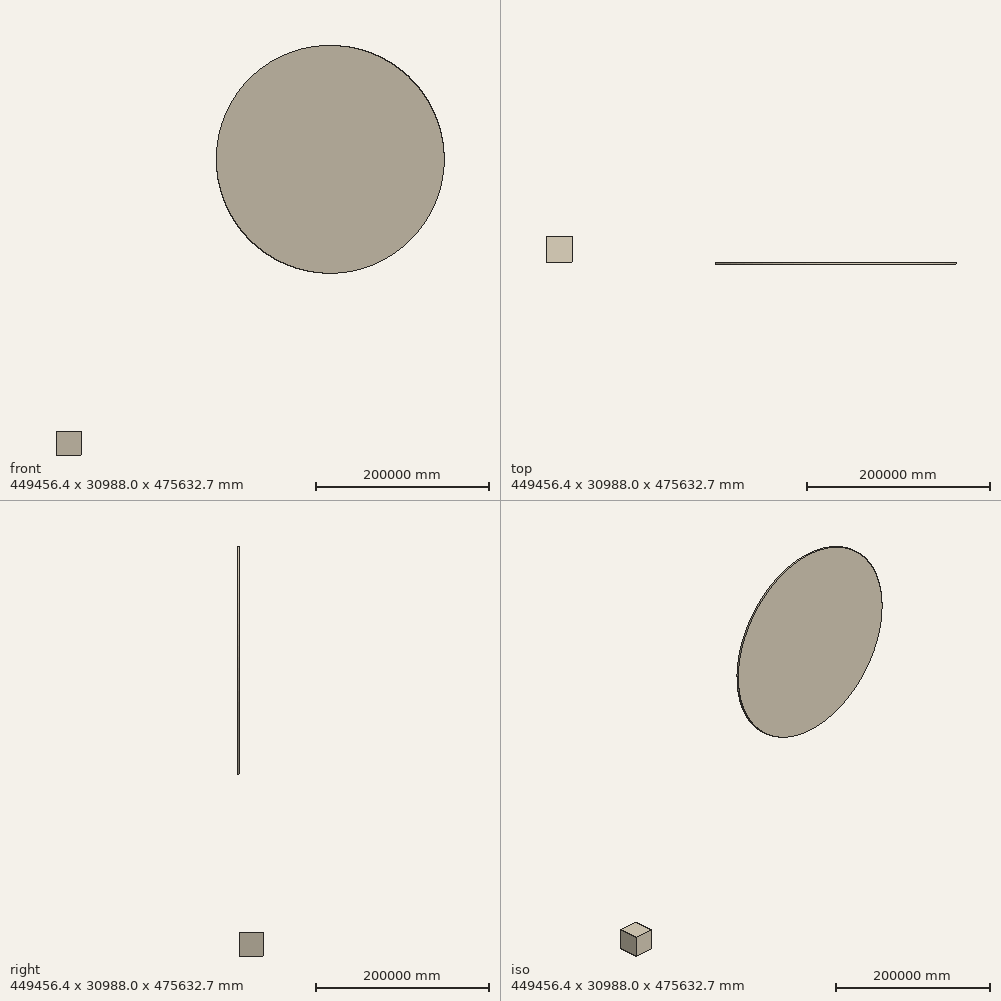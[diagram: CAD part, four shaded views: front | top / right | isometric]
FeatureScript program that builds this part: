
annotation { "Feature Type Name" : "Feature", "Feature Type Description" : "" }
export const myFeature = defineFeature(function(context is Context, id is Id, definition is map)
    precondition{}
    {
        {
            var Q0;
            Q0=qCreatedBy(makeId("Front.planeOp"),FACE);
            var sketch = newSketch(context, id + "F0", { "sketchPlane" : qUnion([Q0])});
            skLineSegment(sketch, "E0.bottom", {"start": v(-481.34, -157.95) * mm, "end": v(-375.42, -157.95) * mm});
            skLineSegment(sketch, "E0.top", {"start": v(-481.34, -331.36) * mm, "end": v(-375.42, -331.36) * mm});
            skLineSegment(sketch, "E0.left", {"start": v(-481.34, -157.95) * mm, "end": v(-481.34, -331.36) * mm});
            skLineSegment(sketch, "E0.right", {"start": v(-375.42, -157.95) * mm, "end": v(-375.42, -331.36) * mm});
            skSolve(sketch);
        }
        {
            var Q0;
            Q0=makeQuery(id+"F0.imprint","IMPRINT",FACE,{"disambiguationData":[TD([[makeQuery(id+"F0.imprint","IMPRINT",EDGE,{"derivedFrom":sQuery(id+"F0.wireOp",EDGE,"E0.bottom")}),-1.0]])]});
            extrude(context, id + "F1", {"entities" : qUnion([Q0]), "depth" : 508 * mm});
        }
        {
            var Q0;
            Q0=makeQuery(id+"F1.opExtrude","SWEPT_FACE",FACE,{"disambiguationData":[OSD([sQuery(id+"F0.wireOp",EDGE,"E0.bottom")])]});
            extrude(context, id + "F2", {"entities" : qUnion([Q0]), "operationType" : NewBodyOperationType.ADD, "depth" : 254 * mm});
        }
        {
            var Q0;
            {var subQ0=sQuery(id+"F0.wireOp",EDGE,"E0.right");Q0=makeQuery(id+"F2.boolean.opBoolean","MERGE",FACE,{"derivedFrom":[makeQuery(id+"F1.opExtrude","SWEPT_FACE",FACE,{"disambiguationData":[OSD([subQ0])]}),makeQuery(id+"F2.opExtrude","SWEPT_FACE",FACE,{"disambiguationData":[OSD([sQuery(id+"F0.wireOp",EDGE,"E0.bottom"),subQ0])]})]});}
            extrude(context, id + "F3", {"entities" : qUnion([Q0]), "operationType" : NewBodyOperationType.ADD, "depth" : 254 * mm});
        }
        {
            var Q0;
            {var subQ0=sQuery(id+"F0.wireOp",EDGE,"E0.right");var subQ1=sQuery(id+"F0.wireOp",EDGE,"E0.bottom");Q0=makeQuery(id+"F3.boolean.opBoolean","MERGE",FACE,{"derivedFrom":[makeQuery(id+"F2.opExtrude","CAP_FACE",FACE,{"disambiguationData":[OSD([subQ1])],"isStart":false}),makeQuery(id+"F3.opExtrude","SWEPT_FACE",FACE,{"disambiguationData":[OSD([subQ1,subQ0]),TDD([makeQuery(id+"F2.opExtrude","CAP_EDGE",EDGE,{"disambiguationData":[OSD([subQ1,subQ0])],"isStart":false})])]})]});}
            extrude(context, id + "F4", {"entities" : qUnion([Q0]), "operationType" : NewBodyOperationType.ADD, "depth" : 2540 * mm});
        }
        {
            var Q0;
            {var subQ0=sQuery(id+"F0.wireOp",EDGE,"E0.right");var subQ1=sQuery(id+"F0.wireOp",EDGE,"E0.bottom");Q0=makeQuery(id+"F4.boolean.opBoolean","MERGE",FACE,{"derivedFrom":[makeQuery(id+"F3.opExtrude","CAP_FACE",FACE,{"disambiguationData":[OSD([subQ1,subQ0])],"isStart":false}),makeQuery(id+"F4.opExtrude","SWEPT_FACE",FACE,{"disambiguationData":[OSD([subQ1,subQ0]),TDD([makeQuery(id+"F3.opExtrude","CAP_EDGE",EDGE,{"disambiguationData":[OSD([subQ1,subQ0]),TDD([makeQuery(id+"F2.opExtrude","CAP_EDGE",EDGE,{"disambiguationData":[OSD([subQ1,subQ0])],"isStart":false})])],"isStart":false})])]})]});}
            extrude(context, id + "F5", {"entities" : qUnion([Q0]), "operationType" : NewBodyOperationType.ADD, "depth" : 2540 * mm});
        }
        {
            var Q0;
            {var subQ0=sQuery(id+"F0.wireOp",EDGE,"E0.right");var subQ1=sQuery(id+"F0.wireOp",EDGE,"E0.bottom");var subQ2=makeQuery(id+"F1.opExtrude","CAP_VERTEX",VERTEX,{"disambiguationData":[OSD([subQ1,subQ0])],"isStart":false});var subQ3=makeQuery(id+"F2.opExtrude","CAP_VERTEX",VERTEX,{"disambiguationData":[OSD([subQ1,subQ0]),TDD([subQ2])],"isStart":false});var subQ4=makeQuery(id+"F2.boolean.opBoolean","MERGE",EDGE,{"derivedFrom":[makeQuery(id+"F1.opExtrude","CAP_EDGE",EDGE,{"disambiguationData":[OSD([subQ0])],"isStart":false}),makeQuery(id+"F2.opExtrude","SWEPT_EDGE",EDGE,{"disambiguationData":[OSD([subQ1,subQ0]),TDD([subQ2])]})]});var subQ5=makeQuery(id+"F1.opExtrude","CAP_EDGE",EDGE,{"disambiguationData":[OSD([subQ1])],"isStart":false});Q0=makeQuery(id+"F5.boolean.opBoolean","MERGE",FACE,{"derivedFrom":[makeQuery(id+"F4.boolean.opBoolean","MERGE",FACE,{"derivedFrom":[makeQuery(id+"F3.boolean.opBoolean","MERGE",FACE,{"derivedFrom":[makeQuery(id+"F2.boolean.opBoolean","MERGE",FACE,{"derivedFrom":[makeQuery(id+"F1.opExtrude","CAP_FACE",FACE,{"disambiguationData":[OSD([subQ1,sQuery(id+"F0.wireOp",EDGE,"E0.top"),sQuery(id+"F0.wireOp",EDGE,"E0.left"),subQ0])],"isStart":false}),makeQuery(id+"F2.opExtrude","SWEPT_FACE",FACE,{"disambiguationData":[OSD([subQ1]),TDD([subQ5])]})]}),makeQuery(id+"F3.opExtrude","SWEPT_FACE",FACE,{"disambiguationData":[OSD([subQ1,subQ0]),TDD([subQ4])]})]}),makeQuery(id+"F4.opExtrude","SWEPT_FACE",FACE,{"disambiguationData":[OSD([subQ1,subQ0]),TDD([makeQuery(id+"F3.boolean.opBoolean","MERGE",EDGE,{"derivedFrom":[makeQuery(id+"F2.opExtrude","CAP_EDGE",EDGE,{"disambiguationData":[OSD([subQ1]),TDD([subQ5])],"isStart":false}),makeQuery(id+"F3.opExtrude","SWEPT_EDGE",EDGE,{"disambiguationData":[OSD([subQ1,subQ0]),TDD([subQ3])]})]})])]})]}),makeQuery(id+"F5.opExtrude","SWEPT_FACE",FACE,{"disambiguationData":[OSD([subQ1,subQ0]),TDD([makeQuery(id+"F4.boolean.opBoolean","MERGE",EDGE,{"derivedFrom":[makeQuery(id+"F3.opExtrude","CAP_EDGE",EDGE,{"disambiguationData":[OSD([subQ1,subQ0]),TDD([subQ4])],"isStart":false}),makeQuery(id+"F4.opExtrude","SWEPT_EDGE",EDGE,{"disambiguationData":[OSD([subQ1,subQ0]),TDD([makeQuery(id+"F3.opExtrude","CAP_VERTEX",VERTEX,{"disambiguationData":[OSD([subQ1,subQ0]),TDD([subQ3])],"isStart":false})])]})]})])]})]});}
            extrude(context, id + "F6", {"entities" : qUnion([Q0]), "operationType" : NewBodyOperationType.ADD, "depth" : 2540 * mm});
        }
        {
            var Q0;
            Q0=makeQuery(id+"F6.opExtrude","CAP_FACE",FACE,{"disambiguationData":[OSD([sQuery(id+"F0.wireOp",EDGE,"E0.bottom"),sQuery(id+"F0.wireOp",EDGE,"E0.top"),sQuery(id+"F0.wireOp",EDGE,"E0.left"),sQuery(id+"F0.wireOp",EDGE,"E0.right")])],"isStart":false});
            extrude(context, id + "F7", {"entities" : qUnion([Q0]), "operationType" : NewBodyOperationType.ADD, "depth" : 25400 * mm});
        }
        {
            var Q0;
            {var subQ0=sQuery(id+"F0.wireOp",EDGE,"E0.right");var subQ1=sQuery(id+"F0.wireOp",EDGE,"E0.bottom");var subQ2=makeQuery(id+"F2.opExtrude","CAP_VERTEX",VERTEX,{"disambiguationData":[OSD([subQ1,subQ0]),TDD([makeQuery(id+"F1.opExtrude","CAP_VERTEX",VERTEX,{"disambiguationData":[OSD([subQ1,subQ0])],"isStart":false})])],"isStart":false});var subQ3=makeQuery(id+"F5.boolean.opBoolean","MERGE",EDGE,{"derivedFrom":[makeQuery(id+"F4.opExtrude","CAP_EDGE",EDGE,{"disambiguationData":[OSD([subQ1,subQ0]),TDD([makeQuery(id+"F3.boolean.opBoolean","MERGE",EDGE,{"derivedFrom":[makeQuery(id+"F2.opExtrude","CAP_EDGE",EDGE,{"disambiguationData":[OSD([subQ1]),TDD([makeQuery(id+"F1.opExtrude","CAP_EDGE",EDGE,{"disambiguationData":[OSD([subQ1])],"isStart":false})])],"isStart":false}),makeQuery(id+"F3.opExtrude","SWEPT_EDGE",EDGE,{"disambiguationData":[OSD([subQ1,subQ0]),TDD([subQ2])]})]})])],"isStart":false}),makeQuery(id+"F5.opExtrude","SWEPT_EDGE",EDGE,{"disambiguationData":[OSD([subQ1,subQ0]),TDD([makeQuery(id+"F4.opExtrude","CAP_VERTEX",VERTEX,{"disambiguationData":[OSD([subQ1,subQ0]),TDD([makeQuery(id+"F3.opExtrude","CAP_VERTEX",VERTEX,{"disambiguationData":[OSD([subQ1,subQ0]),TDD([subQ2])],"isStart":false})])],"isStart":false})])]})]});Q0=makeQuery(id+"F7.boolean.opBoolean","MERGE",FACE,{"derivedFrom":[makeQuery(id+"F6.boolean.opBoolean","MERGE",FACE,{"derivedFrom":[makeQuery(id+"F5.boolean.opBoolean","MERGE",FACE,{"derivedFrom":[makeQuery(id+"F4.opExtrude","CAP_FACE",FACE,{"disambiguationData":[OSD([subQ1,subQ0])],"isStart":false}),makeQuery(id+"F5.opExtrude","SWEPT_FACE",FACE,{"disambiguationData":[OSD([subQ1,subQ0]),TDD([makeQuery(id+"F4.opExtrude","CAP_EDGE",EDGE,{"disambiguationData":[OSD([subQ1,subQ0]),TDD([makeQuery(id+"F3.opExtrude","CAP_EDGE",EDGE,{"disambiguationData":[OSD([subQ1,subQ0]),TDD([makeQuery(id+"F2.opExtrude","CAP_EDGE",EDGE,{"disambiguationData":[OSD([subQ1,subQ0])],"isStart":false})])],"isStart":false})])],"isStart":false})])]})]}),makeQuery(id+"F6.opExtrude","SWEPT_FACE",FACE,{"disambiguationData":[OSD([subQ1,subQ0]),TDD([subQ3])]})]}),makeQuery(id+"F7.opExtrude","SWEPT_FACE",FACE,{"disambiguationData":[OSD([subQ1,subQ0]),TDD([makeQuery(id+"F6.opExtrude","CAP_EDGE",EDGE,{"disambiguationData":[OSD([subQ1,subQ0]),TDD([subQ3])],"isStart":false})])]})]});}
            extrude(context, id + "F8", {"entities" : qUnion([Q0]), "operationType" : NewBodyOperationType.ADD, "depth" : 25400 * mm});
        }
        {
            var Q0;
            {var subQ0=sQuery(id+"F0.wireOp",EDGE,"E0.right");var subQ1=sQuery(id+"F0.wireOp",EDGE,"E0.bottom");var subQ2=makeQuery(id+"F1.opExtrude","CAP_VERTEX",VERTEX,{"disambiguationData":[OSD([subQ1,subQ0])],"isStart":false});var subQ3=makeQuery(id+"F5.opExtrude","CAP_EDGE",EDGE,{"disambiguationData":[OSD([subQ1,subQ0]),TDD([makeQuery(id+"F4.boolean.opBoolean","MERGE",EDGE,{"derivedFrom":[makeQuery(id+"F3.opExtrude","CAP_EDGE",EDGE,{"disambiguationData":[OSD([subQ1,subQ0]),TDD([makeQuery(id+"F2.boolean.opBoolean","MERGE",EDGE,{"derivedFrom":[makeQuery(id+"F1.opExtrude","CAP_EDGE",EDGE,{"disambiguationData":[OSD([subQ0])],"isStart":false}),makeQuery(id+"F2.opExtrude","SWEPT_EDGE",EDGE,{"disambiguationData":[OSD([subQ1,subQ0]),TDD([subQ2])]})]})])],"isStart":false}),makeQuery(id+"F4.opExtrude","SWEPT_EDGE",EDGE,{"disambiguationData":[OSD([subQ1,subQ0]),TDD([makeQuery(id+"F3.opExtrude","CAP_VERTEX",VERTEX,{"disambiguationData":[OSD([subQ1,subQ0]),TDD([makeQuery(id+"F2.opExtrude","CAP_VERTEX",VERTEX,{"disambiguationData":[OSD([subQ1,subQ0]),TDD([subQ2])],"isStart":false})])],"isStart":false})])]})]})])],"isStart":false});Q0=makeQuery(id+"F8.boolean.opBoolean","MERGE",FACE,{"derivedFrom":[makeQuery(id+"F7.boolean.opBoolean","MERGE",FACE,{"derivedFrom":[makeQuery(id+"F6.boolean.opBoolean","MERGE",FACE,{"derivedFrom":[makeQuery(id+"F5.opExtrude","CAP_FACE",FACE,{"disambiguationData":[OSD([subQ1,subQ0])],"isStart":false}),makeQuery(id+"F6.opExtrude","SWEPT_FACE",FACE,{"disambiguationData":[OSD([subQ1,subQ0]),TDD([subQ3])]})]}),makeQuery(id+"F7.opExtrude","SWEPT_FACE",FACE,{"disambiguationData":[OSD([subQ1,subQ0]),TDD([makeQuery(id+"F6.opExtrude","CAP_EDGE",EDGE,{"disambiguationData":[OSD([subQ1,subQ0]),TDD([subQ3])],"isStart":false})])]})]}),makeQuery(id+"F8.opExtrude","SWEPT_FACE",FACE,{"disambiguationData":[OSD([subQ1,subQ0]),TDD([makeQuery(id+"F7.boolean.opBoolean","MERGE",EDGE,{"derivedFrom":[makeQuery(id+"F6.boolean.opBoolean","MERGE",EDGE,{"derivedFrom":[makeQuery(id+"F5.opExtrude","CAP_EDGE",EDGE,{"disambiguationData":[OSD([subQ1,subQ0]),TDD([makeQuery(id+"F4.opExtrude","CAP_EDGE",EDGE,{"disambiguationData":[OSD([subQ1,subQ0]),TDD([makeQuery(id+"F3.opExtrude","CAP_EDGE",EDGE,{"disambiguationData":[OSD([subQ1,subQ0]),TDD([makeQuery(id+"F2.opExtrude","CAP_EDGE",EDGE,{"disambiguationData":[OSD([subQ1,subQ0])],"isStart":false})])],"isStart":false})])],"isStart":false})])],"isStart":false}),makeQuery(id+"F6.opExtrude","SWEPT_EDGE",EDGE,{"disambiguationData":[OSD([subQ1,subQ0])]})]}),makeQuery(id+"F7.opExtrude","SWEPT_EDGE",EDGE,{"disambiguationData":[OSD([subQ1,subQ0])]})]})])]})]});}
            extrude(context, id + "F9", {"entities" : qUnion([Q0]), "operationType" : NewBodyOperationType.ADD, "depth" : 25400 * mm});
        }
        {
            var Q0;
            Q0=makeQuery(id+"F9.opExtrude","CAP_FACE",FACE,{"disambiguationData":[OSD([sQuery(id+"F0.wireOp",EDGE,"E0.bottom"),sQuery(id+"F0.wireOp",EDGE,"E0.right")])],"isStart":false});
            var sketch = newSketch(context, id + "F10", { "sketchPlane" : qUnion([Q0])});
            skSolve(sketch);
        }
        {
            var Q0;
            {var subQ0=sQuery(id+"F0.wireOp",EDGE,"E0.right");Q0=makeQuery(id+"F10.imprint","IMPRINT",FACE,{"disambiguationData":[TD([[makeQuery(id+"F10.imprint","IMPRINT",EDGE,{"derivedFrom":makeQuery(id+"F9.opExtrude","CAP_EDGE",EDGE,{"disambiguationData":[OSD([sQuery(id+"F0.wireOp",EDGE,"E0.top"),subQ0])],"isStart":false})}),1.0]])]});}
            var sketch = newSketch(context, id + "F11", { "sketchPlane" : qUnion([Q0])});
            skSolve(sketch);
        }
        {
            var Q0;
            {var subQ0=sQuery(id+"F0.wireOp",EDGE,"E0.right");Q0=makeQuery(id+"F10.imprint","IMPRINT",FACE,{"disambiguationData":[TD([[makeQuery(id+"F10.imprint","IMPRINT",EDGE,{"derivedFrom":makeQuery(id+"F9.opExtrude","CAP_EDGE",EDGE,{"disambiguationData":[OSD([sQuery(id+"F0.wireOp",EDGE,"E0.top"),subQ0])],"isStart":false})}),1.0]])]});}
            extrude(context, id + "F12", {"entities" : qUnion([Q0]), "operationType" : NewBodyOperationType.ADD, "depth" : 25.4 * mm});
        }
        {
            var Q0;
            {var subQ0=sQuery(id+"F0.wireOp",EDGE,"E0.right");var subQ1=sQuery(id+"F0.wireOp",EDGE,"E0.bottom");var subQ2=makeQuery(id+"F8.opExtrude","CAP_EDGE",EDGE,{"disambiguationData":[OSD([subQ1,subQ0]),TDD([makeQuery(id+"F7.boolean.opBoolean","MERGE",EDGE,{"derivedFrom":[makeQuery(id+"F6.boolean.opBoolean","MERGE",EDGE,{"derivedFrom":[makeQuery(id+"F5.opExtrude","CAP_EDGE",EDGE,{"disambiguationData":[OSD([subQ1,subQ0]),TDD([makeQuery(id+"F4.opExtrude","CAP_EDGE",EDGE,{"disambiguationData":[OSD([subQ1,subQ0]),TDD([makeQuery(id+"F3.opExtrude","CAP_EDGE",EDGE,{"disambiguationData":[OSD([subQ1,subQ0]),TDD([makeQuery(id+"F2.opExtrude","CAP_EDGE",EDGE,{"disambiguationData":[OSD([subQ1,subQ0])],"isStart":false})])],"isStart":false})])],"isStart":false})])],"isStart":false}),makeQuery(id+"F6.opExtrude","SWEPT_EDGE",EDGE,{"disambiguationData":[OSD([subQ1,subQ0])]})]}),makeQuery(id+"F7.opExtrude","SWEPT_EDGE",EDGE,{"disambiguationData":[OSD([subQ1,subQ0])]})]})])],"isStart":false});Q0=makeQuery(id+"F12.boolean.opBoolean","MERGE",FACE,{"derivedFrom":[makeQuery(id+"F9.boolean.opBoolean","MERGE",FACE,{"derivedFrom":[makeQuery(id+"F8.opExtrude","CAP_FACE",FACE,{"disambiguationData":[OSD([subQ1,subQ0])],"isStart":false}),makeQuery(id+"F9.opExtrude","SWEPT_FACE",FACE,{"disambiguationData":[OSD([subQ1,subQ0]),TDD([subQ2])]})]}),makeQuery(id+"F12.opExtrude","SWEPT_FACE",FACE,{"disambiguationData":[OSD([subQ1,subQ0]),TDD([makeQuery(id+"F10.imprint","IMPRINT",EDGE,{"derivedFrom":makeQuery(id+"F9.opExtrude","CAP_EDGE",EDGE,{"disambiguationData":[OSD([subQ1,subQ0]),TDD([subQ2])],"isStart":false})})])]})]});}
            var sketch = newSketch(context, id + "F13", { "sketchPlane" : qUnion([Q0])});
            skSolve(sketch);
        }
        {
            var Q0;
            {var subQ0=sQuery(id+"F0.wireOp",EDGE,"E0.bottom");Q0=makeQuery(id+"F13.imprint","IMPRINT",FACE,{"disambiguationData":[TD([[makeQuery(id+"F13.imprint","IMPRINT",EDGE,{"derivedFrom":makeQuery(id+"F8.opExtrude","CAP_EDGE",EDGE,{"disambiguationData":[OSD([subQ0,sQuery(id+"F0.wireOp",EDGE,"E0.left")])],"isStart":false})}),-1.0]])]});}
            var sketch = newSketch(context, id + "F14", { "sketchPlane" : qUnion([Q0])});
            skLineSegment(sketch, "E1.bottom", {"start": v(2166.14, -15440.6) * mm, "end": v(7362.03, -15440.6) * mm});
            skLineSegment(sketch, "E1.top", {"start": v(2166.14, -24936.56) * mm, "end": v(7362.03, -24936.56) * mm});
            skLineSegment(sketch, "E1.left", {"start": v(2166.14, -15440.6) * mm, "end": v(2166.14, -24936.56) * mm});
            skLineSegment(sketch, "E1.right", {"start": v(7362.03, -15440.6) * mm, "end": v(7362.03, -24936.56) * mm});
            skLineSegment(sketch, "E2.bottom", {"start": v(7362.03, -11140.55) * mm, "end": v(17395.49, -11140.55) * mm});
            skLineSegment(sketch, "E2.top", {"start": v(7362.03, -15440.6) * mm, "end": v(17395.49, -15440.6) * mm});
            skLineSegment(sketch, "E2.left", {"start": v(7362.03, -11140.55) * mm, "end": v(7362.03, -15440.6) * mm});
            skLineSegment(sketch, "E2.right", {"start": v(17395.49, -11140.55) * mm, "end": v(17395.49, -15440.6) * mm});
            skLineSegment(sketch, "E3.bottom", {"start": v(17395.49, -15440.6) * mm, "end": v(22322.63, -15440.6) * mm});
            skLineSegment(sketch, "E3.top", {"start": v(17395.49, -24399.05) * mm, "end": v(22322.63, -24399.05) * mm});
            skLineSegment(sketch, "E3.left", {"start": v(17395.49, -15440.6) * mm, "end": v(17395.49, -24399.05) * mm});
            skLineSegment(sketch, "E3.right", {"start": v(22322.63, -15440.6) * mm, "end": v(22322.63, -24399.05) * mm});
            skLineSegment(sketch, "E4.bottom", {"start": v(4047.4, -1734.2) * mm, "end": v(8705.8, -1734.2) * mm});
            skLineSegment(sketch, "E4.top", {"start": v(4047.4, -9169.7) * mm, "end": v(8705.8, -9169.7) * mm});
            skLineSegment(sketch, "E4.left", {"start": v(4047.4, -1734.2) * mm, "end": v(4047.4, -9169.7) * mm});
            skLineSegment(sketch, "E4.right", {"start": v(8705.8, -1734.2) * mm, "end": v(8705.8, -9169.7) * mm});
            skLineSegment(sketch, "E5.bottom", {"start": v(15603.8, -1465.44) * mm, "end": v(20799.7, -1465.44) * mm});
            skLineSegment(sketch, "E5.top", {"start": v(15603.8, -9617.62) * mm, "end": v(20799.7, -9617.62) * mm});
            skLineSegment(sketch, "E5.left", {"start": v(15603.8, -1465.44) * mm, "end": v(15603.8, -9617.62) * mm});
            skLineSegment(sketch, "E5.right", {"start": v(20799.7, -1465.44) * mm, "end": v(20799.7, -9617.62) * mm});
            skSolve(sketch);
        }
        {
            var Q0;
            {var subQ0=sQuery(id+"F0.wireOp",EDGE,"E0.bottom");Q0=makeQuery(id+"F13.imprint","IMPRINT",FACE,{"disambiguationData":[TD([[makeQuery(id+"F13.imprint","IMPRINT",EDGE,{"derivedFrom":makeQuery(id+"F8.opExtrude","CAP_EDGE",EDGE,{"disambiguationData":[OSD([subQ0,sQuery(id+"F0.wireOp",EDGE,"E0.left")])],"isStart":false})}),-1.0]])]});}
            extrude(context, id + "F15", {"entities" : qUnion([Q0]), "operationType" : NewBodyOperationType.ADD, "endBound" : BoundingType.SYMMETRIC, "depth" : 25.4 * mm});
        }
        {
            var Q0;
            {var subQ0=sQuery(id+"F0.wireOp",EDGE,"E0.right");var subQ1=sQuery(id+"F0.wireOp",EDGE,"E0.bottom");var subQ2=makeQuery(id+"F7.opExtrude","CAP_VERTEX",VERTEX,{"disambiguationData":[OSD([subQ1,subQ0])],"isStart":false});var subQ3=makeQuery(id+"F1.opExtrude","CAP_VERTEX",VERTEX,{"disambiguationData":[OSD([subQ1,subQ0])],"isStart":false});var subQ4=makeQuery(id+"F2.opExtrude","CAP_VERTEX",VERTEX,{"disambiguationData":[OSD([subQ1,subQ0]),TDD([subQ3])],"isStart":false});var subQ5=makeQuery(id+"F3.opExtrude","CAP_VERTEX",VERTEX,{"disambiguationData":[OSD([subQ1,subQ0]),TDD([subQ4])],"isStart":false});var subQ6=makeQuery(id+"F8.boolean.opBoolean","MERGE",EDGE,{"derivedFrom":[makeQuery(id+"F7.opExtrude","CAP_EDGE",EDGE,{"disambiguationData":[OSD([subQ1,subQ0]),TDD([makeQuery(id+"F6.opExtrude","CAP_EDGE",EDGE,{"disambiguationData":[OSD([subQ1,subQ0]),TDD([makeQuery(id+"F5.opExtrude","CAP_EDGE",EDGE,{"disambiguationData":[OSD([subQ1,subQ0]),TDD([makeQuery(id+"F4.boolean.opBoolean","MERGE",EDGE,{"derivedFrom":[makeQuery(id+"F3.opExtrude","CAP_EDGE",EDGE,{"disambiguationData":[OSD([subQ1,subQ0]),TDD([makeQuery(id+"F2.boolean.opBoolean","MERGE",EDGE,{"derivedFrom":[makeQuery(id+"F1.opExtrude","CAP_EDGE",EDGE,{"disambiguationData":[OSD([subQ0])],"isStart":false}),makeQuery(id+"F2.opExtrude","SWEPT_EDGE",EDGE,{"disambiguationData":[OSD([subQ1,subQ0]),TDD([subQ3])]})]})])],"isStart":false}),makeQuery(id+"F4.opExtrude","SWEPT_EDGE",EDGE,{"disambiguationData":[OSD([subQ1,subQ0]),TDD([subQ5])]})]})])],"isStart":false})])],"isStart":false})])],"isStart":false}),makeQuery(id+"F8.opExtrude","SWEPT_EDGE",EDGE,{"disambiguationData":[OSD([subQ1,subQ0]),TDD([subQ2])]})]});var subQ7=makeQuery(id+"F9.opExtrude","CAP_EDGE",EDGE,{"disambiguationData":[OSD([subQ1,subQ0]),TDD([subQ6])],"isStart":false});var subQ8=makeQuery(id+"F7.opExtrude","CAP_EDGE",EDGE,{"disambiguationData":[OSD([subQ1,subQ0]),TDD([makeQuery(id+"F6.opExtrude","CAP_EDGE",EDGE,{"disambiguationData":[OSD([subQ1,subQ0]),TDD([makeQuery(id+"F5.boolean.opBoolean","MERGE",EDGE,{"derivedFrom":[makeQuery(id+"F4.opExtrude","CAP_EDGE",EDGE,{"disambiguationData":[OSD([subQ1,subQ0]),TDD([makeQuery(id+"F3.boolean.opBoolean","MERGE",EDGE,{"derivedFrom":[makeQuery(id+"F2.opExtrude","CAP_EDGE",EDGE,{"disambiguationData":[OSD([subQ1]),TDD([makeQuery(id+"F1.opExtrude","CAP_EDGE",EDGE,{"disambiguationData":[OSD([subQ1])],"isStart":false})])],"isStart":false}),makeQuery(id+"F3.opExtrude","SWEPT_EDGE",EDGE,{"disambiguationData":[OSD([subQ1,subQ0]),TDD([subQ4])]})]})])],"isStart":false}),makeQuery(id+"F5.opExtrude","SWEPT_EDGE",EDGE,{"disambiguationData":[OSD([subQ1,subQ0]),TDD([makeQuery(id+"F4.opExtrude","CAP_VERTEX",VERTEX,{"disambiguationData":[OSD([subQ1,subQ0]),TDD([subQ5])],"isStart":false})])]})]})])],"isStart":false})])],"isStart":false});Q0=makeQuery(id+"F15.boolean.opBoolean","MERGE",FACE,{"derivedFrom":[makeQuery(id+"F12.boolean.opBoolean","MERGE",FACE,{"derivedFrom":[makeQuery(id+"F9.boolean.opBoolean","MERGE",FACE,{"derivedFrom":[makeQuery(id+"F8.boolean.opBoolean","MERGE",FACE,{"derivedFrom":[makeQuery(id+"F7.opExtrude","CAP_FACE",FACE,{"disambiguationData":[OSD([subQ1,sQuery(id+"F0.wireOp",EDGE,"E0.top"),sQuery(id+"F0.wireOp",EDGE,"E0.left"),subQ0])],"isStart":false}),makeQuery(id+"F8.opExtrude","SWEPT_FACE",FACE,{"disambiguationData":[OSD([subQ1,subQ0]),TDD([subQ8])]})]}),makeQuery(id+"F9.opExtrude","SWEPT_FACE",FACE,{"disambiguationData":[OSD([subQ1,subQ0]),TDD([subQ6])]})]}),makeQuery(id+"F12.opExtrude","SWEPT_FACE",FACE,{"disambiguationData":[OSD([subQ1,subQ0]),TDD([makeQuery(id+"F10.imprint","IMPRINT",EDGE,{"derivedFrom":subQ7})])]})]}),makeQuery(id+"F15.opExtrude","SWEPT_FACE",FACE,{"disambiguationData":[OSD([subQ1,subQ0]),TDD([makeQuery(id+"F13.imprint","IMPRINT",EDGE,{"derivedFrom":makeQuery(id+"F12.boolean.opBoolean","MERGE",EDGE,{"derivedFrom":[makeQuery(id+"F9.boolean.opBoolean","MERGE",EDGE,{"derivedFrom":[makeQuery(id+"F8.opExtrude","CAP_EDGE",EDGE,{"disambiguationData":[OSD([subQ1,subQ0]),TDD([subQ8])],"isStart":false}),makeQuery(id+"F9.opExtrude","SWEPT_EDGE",EDGE,{"disambiguationData":[OSD([subQ1,subQ0]),TDD([makeQuery(id+"F8.opExtrude","CAP_VERTEX",VERTEX,{"disambiguationData":[OSD([subQ1,subQ0]),TDD([subQ2])],"isStart":false})])]})]}),makeQuery(id+"F12.opExtrude","SWEPT_EDGE",EDGE,{"disambiguationData":[OSD([subQ1,subQ0]),TDD([makeQuery(id+"F10.imprint","INTERSECT",VERTEX,{"derivedFrom":[makeQuery(id+"F9.opExtrude","CAP_EDGE",EDGE,{"disambiguationData":[OSD([subQ1,subQ0]),TDD([makeQuery(id+"F8.opExtrude","CAP_EDGE",EDGE,{"disambiguationData":[OSD([subQ1,subQ0]),TDD([makeQuery(id+"F7.boolean.opBoolean","MERGE",EDGE,{"derivedFrom":[makeQuery(id+"F6.boolean.opBoolean","MERGE",EDGE,{"derivedFrom":[makeQuery(id+"F5.opExtrude","CAP_EDGE",EDGE,{"disambiguationData":[OSD([subQ1,subQ0]),TDD([makeQuery(id+"F4.opExtrude","CAP_EDGE",EDGE,{"disambiguationData":[OSD([subQ1,subQ0]),TDD([makeQuery(id+"F3.opExtrude","CAP_EDGE",EDGE,{"disambiguationData":[OSD([subQ1,subQ0]),TDD([makeQuery(id+"F2.opExtrude","CAP_EDGE",EDGE,{"disambiguationData":[OSD([subQ1,subQ0])],"isStart":false})])],"isStart":false})])],"isStart":false})])],"isStart":false}),makeQuery(id+"F6.opExtrude","SWEPT_EDGE",EDGE,{"disambiguationData":[OSD([subQ1,subQ0])]})]}),makeQuery(id+"F7.opExtrude","SWEPT_EDGE",EDGE,{"disambiguationData":[OSD([subQ1,subQ0])]})]})])],"isStart":false})])],"isStart":false}),subQ7]})])]})]})})])]})]});}
            var sketch = newSketch(context, id + "F16", { "sketchPlane" : qUnion([Q0])});
            skSolve(sketch);
        }
        {
            var Q0;
            {var subQ0=sQuery(id+"F0.wireOp",EDGE,"E0.right");var subQ1=sQuery(id+"F0.wireOp",EDGE,"E0.bottom");var subQ2=makeQuery(id+"F7.opExtrude","CAP_VERTEX",VERTEX,{"disambiguationData":[OSD([subQ1,subQ0])],"isStart":false});var subQ3=makeQuery(id+"F1.opExtrude","CAP_VERTEX",VERTEX,{"disambiguationData":[OSD([subQ1,subQ0])],"isStart":false});var subQ4=makeQuery(id+"F2.opExtrude","CAP_VERTEX",VERTEX,{"disambiguationData":[OSD([subQ1,subQ0]),TDD([subQ3])],"isStart":false});var subQ5=makeQuery(id+"F3.opExtrude","CAP_VERTEX",VERTEX,{"disambiguationData":[OSD([subQ1,subQ0]),TDD([subQ4])],"isStart":false});var subQ6=makeQuery(id+"F9.opExtrude","CAP_EDGE",EDGE,{"disambiguationData":[OSD([subQ1,subQ0]),TDD([makeQuery(id+"F8.boolean.opBoolean","MERGE",EDGE,{"derivedFrom":[makeQuery(id+"F7.opExtrude","CAP_EDGE",EDGE,{"disambiguationData":[OSD([subQ1,subQ0]),TDD([makeQuery(id+"F6.opExtrude","CAP_EDGE",EDGE,{"disambiguationData":[OSD([subQ1,subQ0]),TDD([makeQuery(id+"F5.opExtrude","CAP_EDGE",EDGE,{"disambiguationData":[OSD([subQ1,subQ0]),TDD([makeQuery(id+"F4.boolean.opBoolean","MERGE",EDGE,{"derivedFrom":[makeQuery(id+"F3.opExtrude","CAP_EDGE",EDGE,{"disambiguationData":[OSD([subQ1,subQ0]),TDD([makeQuery(id+"F2.boolean.opBoolean","MERGE",EDGE,{"derivedFrom":[makeQuery(id+"F1.opExtrude","CAP_EDGE",EDGE,{"disambiguationData":[OSD([subQ0])],"isStart":false}),makeQuery(id+"F2.opExtrude","SWEPT_EDGE",EDGE,{"disambiguationData":[OSD([subQ1,subQ0]),TDD([subQ3])]})]})])],"isStart":false}),makeQuery(id+"F4.opExtrude","SWEPT_EDGE",EDGE,{"disambiguationData":[OSD([subQ1,subQ0]),TDD([subQ5])]})]})])],"isStart":false})])],"isStart":false})])],"isStart":false}),makeQuery(id+"F8.opExtrude","SWEPT_EDGE",EDGE,{"disambiguationData":[OSD([subQ1,subQ0]),TDD([subQ2])]})]})])],"isStart":false});var subQ8=makeQuery(id+"F9.opExtrude","CAP_EDGE",EDGE,{"disambiguationData":[OSD([subQ1,subQ0]),TDD([makeQuery(id+"F8.opExtrude","CAP_EDGE",EDGE,{"disambiguationData":[OSD([subQ1,subQ0]),TDD([makeQuery(id+"F7.boolean.opBoolean","MERGE",EDGE,{"derivedFrom":[makeQuery(id+"F6.boolean.opBoolean","MERGE",EDGE,{"derivedFrom":[makeQuery(id+"F5.opExtrude","CAP_EDGE",EDGE,{"disambiguationData":[OSD([subQ1,subQ0]),TDD([makeQuery(id+"F4.opExtrude","CAP_EDGE",EDGE,{"disambiguationData":[OSD([subQ1,subQ0]),TDD([makeQuery(id+"F3.opExtrude","CAP_EDGE",EDGE,{"disambiguationData":[OSD([subQ1,subQ0]),TDD([makeQuery(id+"F2.opExtrude","CAP_EDGE",EDGE,{"disambiguationData":[OSD([subQ1,subQ0])],"isStart":false})])],"isStart":false})])],"isStart":false})])],"isStart":false}),makeQuery(id+"F6.opExtrude","SWEPT_EDGE",EDGE,{"disambiguationData":[OSD([subQ1,subQ0])]})]}),makeQuery(id+"F7.opExtrude","SWEPT_EDGE",EDGE,{"disambiguationData":[OSD([subQ1,subQ0])]})]})])],"isStart":false})])],"isStart":false});var subQ9=makeQuery(id+"F12.boolean.opBoolean","MERGE",EDGE,{"derivedFrom":[makeQuery(id+"F9.boolean.opBoolean","MERGE",EDGE,{"derivedFrom":[makeQuery(id+"F8.opExtrude","CAP_EDGE",EDGE,{"disambiguationData":[OSD([subQ1,subQ0]),TDD([makeQuery(id+"F7.opExtrude","CAP_EDGE",EDGE,{"disambiguationData":[OSD([subQ1,subQ0]),TDD([makeQuery(id+"F6.opExtrude","CAP_EDGE",EDGE,{"disambiguationData":[OSD([subQ1,subQ0]),TDD([makeQuery(id+"F5.boolean.opBoolean","MERGE",EDGE,{"derivedFrom":[makeQuery(id+"F4.opExtrude","CAP_EDGE",EDGE,{"disambiguationData":[OSD([subQ1,subQ0]),TDD([makeQuery(id+"F3.boolean.opBoolean","MERGE",EDGE,{"derivedFrom":[makeQuery(id+"F2.opExtrude","CAP_EDGE",EDGE,{"disambiguationData":[OSD([subQ1]),TDD([makeQuery(id+"F1.opExtrude","CAP_EDGE",EDGE,{"disambiguationData":[OSD([subQ1])],"isStart":false})])],"isStart":false}),makeQuery(id+"F3.opExtrude","SWEPT_EDGE",EDGE,{"disambiguationData":[OSD([subQ1,subQ0]),TDD([subQ4])]})]})])],"isStart":false}),makeQuery(id+"F5.opExtrude","SWEPT_EDGE",EDGE,{"disambiguationData":[OSD([subQ1,subQ0]),TDD([makeQuery(id+"F4.opExtrude","CAP_VERTEX",VERTEX,{"disambiguationData":[OSD([subQ1,subQ0]),TDD([subQ5])],"isStart":false})])]})]})])],"isStart":false})])],"isStart":false})])],"isStart":false}),makeQuery(id+"F9.opExtrude","SWEPT_EDGE",EDGE,{"disambiguationData":[OSD([subQ1,subQ0]),TDD([makeQuery(id+"F8.opExtrude","CAP_VERTEX",VERTEX,{"disambiguationData":[OSD([subQ1,subQ0]),TDD([subQ2])],"isStart":false})])]})]}),makeQuery(id+"F12.opExtrude","SWEPT_EDGE",EDGE,{"disambiguationData":[OSD([subQ1,subQ0]),TDD([makeQuery(id+"F10.imprint","INTERSECT",VERTEX,{"derivedFrom":[subQ8,subQ6]})])]})]});Q0=makeQuery(id+"F16.imprint","IMPRINT",FACE,{"disambiguationData":[TD([[makeQuery(id+"F16.imprint","IMPRINT",EDGE,{"derivedFrom":makeQuery(id+"F15.opExtrude","CAP_EDGE",EDGE,{"disambiguationData":[OSD([subQ1,subQ0]),TDD([makeQuery(id+"F13.imprint","IMPRINT",EDGE,{"derivedFrom":subQ9})])],"isStart":false})}),-1.0]])]});}
            var sketch = newSketch(context, id + "F17", { "sketchPlane" : qUnion([Q0])});
            skCircle(sketch, "E6", {"center": v(316750.95, 343077.27) * mm, "radius": 132224.08 * mm});
            skSolve(sketch);
        }
        {
            var Q0;
            Q0=makeQuery(id+"F17.imprint","IMPRINT",FACE,{"disambiguationData":[TD([[makeQuery(id+"F17.imprint","IMPRINT",EDGE,{"derivedFrom":sQuery(id+"F17.wireOp",EDGE,"E6")}),1.0]])]});
            extrude(context, id + "F18", {"entities" : qUnion([Q0]), "depth" : 2540 * mm});
        }
    });
